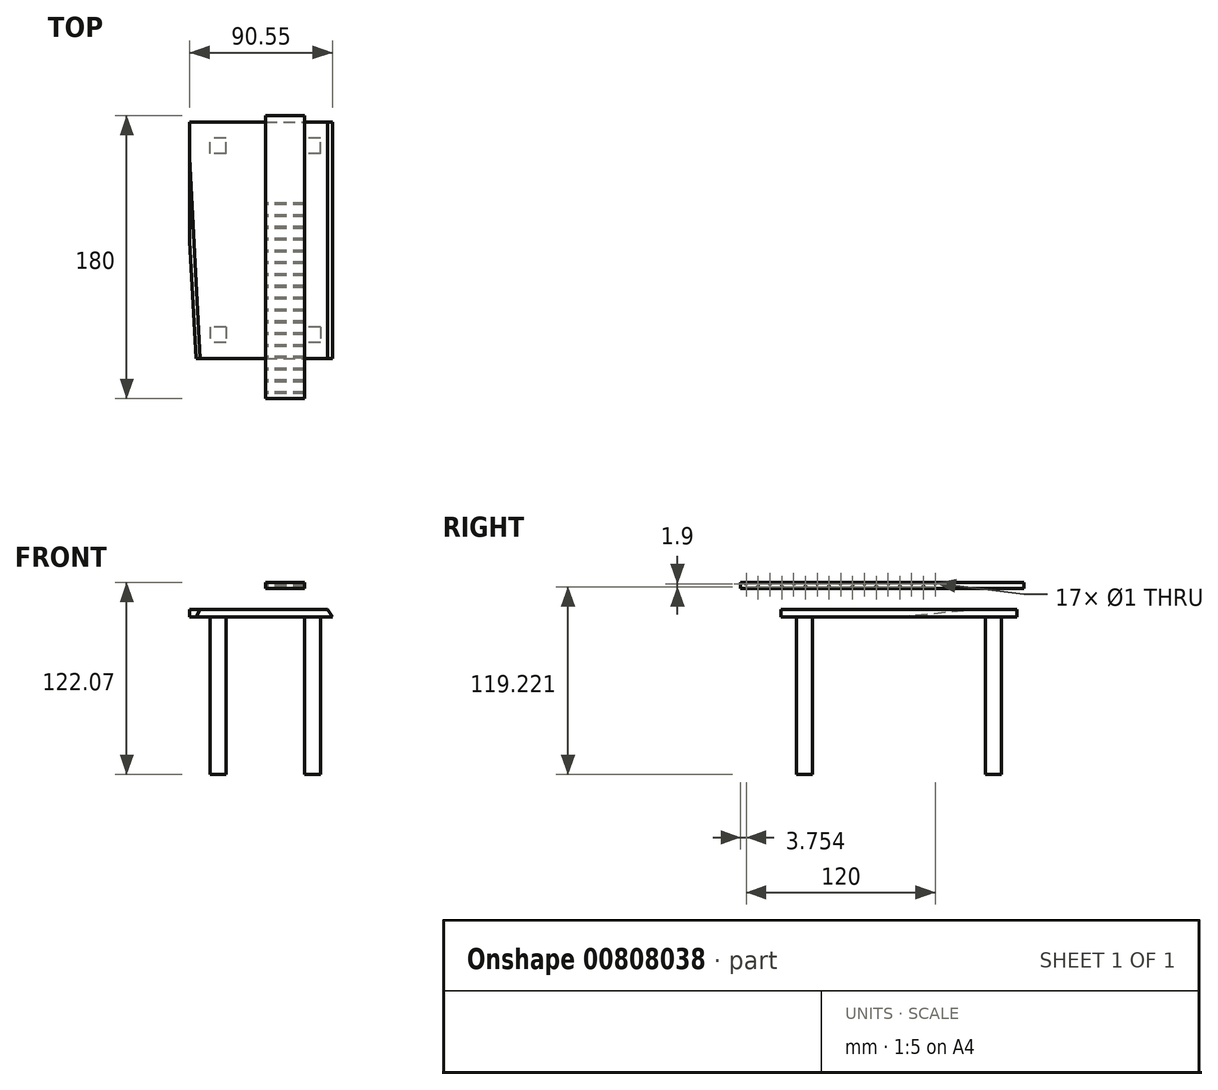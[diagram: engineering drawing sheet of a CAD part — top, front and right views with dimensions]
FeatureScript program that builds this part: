
annotation { "Feature Type Name" : "Feature", "Feature Type Description" : "" }
export const myFeature = defineFeature(function(context is Context, id is Id, definition is map)
    precondition{}
    {
        {
            var Q0;
            Q0=qCreatedBy(makeId("Top.planeOp"),FACE);
            var sketch = newSketch(context, id + "F0", { "sketchPlane" : qUnion([Q0])});
            skLineSegment(sketch, "E0.bottom", {"start": v(0, -75) * mm, "end": v(48, -75) * mm});
            skLineSegment(sketch, "E0.top", {"start": v(0, 75) * mm, "end": v(48, 75) * mm});
            skLineSegment(sketch, "E0.left", {"start": v(0, -75) * mm, "end": v(0, 75) * mm});
            skLineSegment(sketch, "E0.right", {"start": v(48, -75) * mm, "end": v(48, 75) * mm});
            skPoint(sketch, "E0.middle", {"position": v(0, 0) * mm});
            skSolve(sketch);
        }
        {
            var Q0;
            Q0 = qSketchRegion(id + "F0", true);
            extrude(context, id + "F1", {"entities" : qUnion([Q0]), "depth" : 4.8 * mm, "offsetDistance" : 25 * mm});
        }
        {
            var Q0;
            Q0=qCreatedBy(makeId("Top.planeOp"),FACE);
            var sketch = newSketch(context, id + "F2", { "sketchPlane" : qUnion([Q0])});
            skLineSegment(sketch, "E1", {"start": v(48.5, 87.28) * mm, "end": v(40, -75) * mm, "construction": true});
            skLineSegment(sketch, "E2", {"start": v(0, 79.02) * mm, "end": v(0, -87.33) * mm, "construction": true});
            skLineSegment(sketch, "E3", {"start": v(-66.41, -75) * mm, "end": v(-18.41, -75) * mm, "construction": true});
            skSolve(sketch);
        }
        {
            var Q0;
            Q0=sQuery(id+"F2.wireOp",EDGE,"E1");
            cPlane(context, id + "F3", {"entities" : qUnion([Q0]), "cplaneType" : CPlaneType.MID_PLANE, "offset" : 25 * mm, "width" : 150 * mm, "height" : 150 * mm});
        }
        {
            var Q0;
            Q0=qCreatedBy(id+"F3.planeOp",FACE);
            var sketch = newSketch(context, id + "F4", { "sketchPlane" : qUnion([Q0])});
            skLineSegment(sketch, "E4", {"start": v(40.09, 13.64) * mm, "end": v(61.5, 17.13) * mm});
            skLineSegment(sketch, "E5", {"start": v(61.5, 17.13) * mm, "end": v(66.7, -14.02) * mm});
            skLineSegment(sketch, "E6", {"start": v(66.7, -14.02) * mm, "end": v(53.92, -10.31) * mm});
            skLineSegment(sketch, "E7", {"start": v(40.09, 13.64) * mm, "end": v(53.92, -10.31) * mm});
            skSolve(sketch);
        }
        {
            var Q0;
            Q0 = qSketchRegion(id + "F4", true);
            extrude(context, id + "F5", {"entities" : qUnion([Q0]), "operationType" : NewBodyOperationType.REMOVE, "endBound" : BoundingType.THROUGH_ALL, "oppositeDirection" : true, "depth" : 25 * mm, "offsetDistance" : 25 * mm});
        }
        {
            var Q0;
            Q0 = qSketchRegion(id + "F4", true);
            extrude(context, id + "F6", {"entities" : qUnion([Q0]), "operationType" : NewBodyOperationType.REMOVE, "endBound" : BoundingType.THROUGH_ALL, "depth" : 25 * mm, "offsetDistance" : 25 * mm});
        }
        {
            var Q0;
            Q0=makeQuery(id+"F1.opExtrude","SWEPT_BODY",BODY,{"disambiguationData":[OSD([sQuery(id+"F0.wireOp",EDGE,"E0.bottom"),sQuery(id+"F0.wireOp",EDGE,"E0.top"),sQuery(id+"F0.wireOp",EDGE,"E0.left"),sQuery(id+"F0.wireOp",EDGE,"E0.right")])]});
            var Q1;
            Q1=qCreatedBy(makeId("Right.planeOp"),FACE);
            mirror(context, id + "F7", {"operationType" : NewBodyOperationType.ADD, "entities" : qUnion([Q0]), "mirrorPlane" : qUnion([Q1])});
        }
        {
            var Q0;
            {var subQ0=makeQuery(id+"F1.opExtrude","CAP_FACE",FACE,{"disambiguationData":[OSD([sQuery(id+"F0.wireOp",EDGE,"E0.bottom"),sQuery(id+"F0.wireOp",EDGE,"E0.top"),sQuery(id+"F0.wireOp",EDGE,"E0.left"),sQuery(id+"F0.wireOp",EDGE,"E0.right")])],"isStart":true});Q0=makeQuery(id+"F7.boolean.opBoolean","MERGE",FACE,{"derivedFrom":[subQ0,makeQuery(id+"F7.opPattern","COPY",FACE,{"derivedFrom":subQ0,"instanceName":"1"})]});}
            var sketch = newSketch(context, id + "F8", { "sketchPlane" : qUnion([Q0])});
            skLineSegment(sketch, "E8.bottom", {"start": v(30, -60) * mm, "end": v(-30, -60) * mm, "construction": true});
            skLineSegment(sketch, "E8.top", {"start": v(30, 60) * mm, "end": v(-30, 60) * mm, "construction": true});
            skLineSegment(sketch, "E8.left", {"start": v(30, -60) * mm, "end": v(30, 60) * mm, "construction": true});
            skLineSegment(sketch, "E8.right", {"start": v(-30, -60) * mm, "end": v(-30, 60) * mm, "construction": true});
            skPoint(sketch, "E8.middle", {"position": v(0, 0) * mm});
            skLineSegment(sketch, "E9.bottom", {"start": v(-25, 55) * mm, "end": v(-35, 55) * mm});
            skLineSegment(sketch, "E9.top", {"start": v(-25, 65) * mm, "end": v(-35, 65) * mm});
            skLineSegment(sketch, "E9.left", {"start": v(-25, 55) * mm, "end": v(-25, 65) * mm});
            skLineSegment(sketch, "E9.right", {"start": v(-35, 55) * mm, "end": v(-35, 65) * mm});
            skPoint(sketch, "E9.middle", {"position": v(-30, 60) * mm});
            skLineSegment(sketch, "E10.bottom", {"start": v(35, 55) * mm, "end": v(25, 55) * mm});
            skLineSegment(sketch, "E10.top", {"start": v(35, 65) * mm, "end": v(25, 65) * mm});
            skLineSegment(sketch, "E10.left", {"start": v(35, 55) * mm, "end": v(35, 65) * mm});
            skLineSegment(sketch, "E10.right", {"start": v(25, 55) * mm, "end": v(25, 65) * mm});
            skPoint(sketch, "E10.middle", {"position": v(30, 60) * mm});
            skLineSegment(sketch, "E11.bottom", {"start": v(35, -55) * mm, "end": v(25, -55) * mm});
            skLineSegment(sketch, "E11.top", {"start": v(35, -65) * mm, "end": v(25, -65) * mm});
            skLineSegment(sketch, "E11.left", {"start": v(35, -55) * mm, "end": v(35, -65) * mm});
            skLineSegment(sketch, "E11.right", {"start": v(25, -55) * mm, "end": v(25, -65) * mm});
            skPoint(sketch, "E11.middle", {"position": v(30, -60) * mm});
            skLineSegment(sketch, "E12.bottom", {"start": v(-25, -55) * mm, "end": v(-35, -55) * mm});
            skLineSegment(sketch, "E12.top", {"start": v(-25, -65) * mm, "end": v(-35, -65) * mm});
            skLineSegment(sketch, "E12.left", {"start": v(-25, -55) * mm, "end": v(-25, -65) * mm});
            skLineSegment(sketch, "E12.right", {"start": v(-35, -55) * mm, "end": v(-35, -65) * mm});
            skPoint(sketch, "E12.middle", {"position": v(-30, -60) * mm});
            skSolve(sketch);
        }
        {
            var Q0;
            Q0 = qSketchRegion(id + "F8", true);
            extrude(context, id + "F9", {"entities" : qUnion([Q0]), "operationType" : NewBodyOperationType.ADD, "depth" : 100 * mm, "offsetDistance" : 25 * mm});
        }
        {
            var Q0;
            {var subQ0=makeQuery(id+"F1.opExtrude","SWEPT_FACE",FACE,{"disambiguationData":[OSD([sQuery(id+"F0.wireOp",EDGE,"E0.bottom")])]});Q0=makeQuery(id+"F7.boolean.opBoolean","MERGE",FACE,{"derivedFrom":[subQ0,makeQuery(id+"F7.opPattern","COPY",FACE,{"derivedFrom":subQ0,"instanceName":"1"})]});}
            var sketch = newSketch(context, id + "F10", { "sketchPlane" : qUnion([Q0])});
            skLineSegment(sketch, "E13", {"start": v(48.72, -10.13) * mm, "end": v(34.83, 12.68) * mm});
            skLineSegment(sketch, "E14", {"start": v(34.83, 12.68) * mm, "end": v(36.65, 31.45) * mm});
            skLineSegment(sketch, "E15", {"start": v(36.65, 31.45) * mm, "end": v(50.2, 21.12) * mm});
            skLineSegment(sketch, "E16", {"start": v(50.2, 21.12) * mm, "end": v(52.52, -10.3) * mm});
            skLineSegment(sketch, "E17", {"start": v(52.52, -10.3) * mm, "end": v(51.53, -8.98) * mm});
            skLineSegment(sketch, "E18", {"start": v(51.53, -8.98) * mm, "end": v(50.2, -10.46) * mm});
            skLineSegment(sketch, "E19", {"start": v(50.2, -10.46) * mm, "end": v(48.39, -11.95) * mm});
            skLineSegment(sketch, "E20", {"start": v(48.39, -11.95) * mm, "end": v(48.95, -9.76) * mm});
            skLineSegment(sketch, "E21", {"start": v(48.95, -9.76) * mm, "end": v(49, -10.8) * mm});
            skLineSegment(sketch, "E22", {"start": v(49, -10.8) * mm, "end": v(49, -3.85) * mm});
            skLineSegment(sketch, "E23", {"start": v(49, -3.85) * mm, "end": v(48.72, -10.13) * mm});
            skSolve(sketch);
        }
        {
            var Q0;
            Q0 = qSketchRegion(id + "F10", true);
            extrude(context, id + "F11", {"entities" : qUnion([Q0]), "operationType" : NewBodyOperationType.REMOVE, "endBound" : BoundingType.THROUGH_ALL, "oppositeDirection" : true, "depth" : 25 * mm, "offsetDistance" : 25 * mm});
        }
        {
            var Q0;
            Q0=qCreatedBy(makeId("Right.planeOp"),FACE);
            var sketch = newSketch(context, id + "F12", { "sketchPlane" : qUnion([Q0])});
            skLineSegment(sketch, "E24.bottom", {"start": v(-100.67, 22.07) * mm, "end": v(79.33, 22.07) * mm});
            skLineSegment(sketch, "E24.top", {"start": v(-100.67, 18.27) * mm, "end": v(79.33, 18.27) * mm});
            skLineSegment(sketch, "E24.left", {"start": v(-100.67, 22.07) * mm, "end": v(-100.67, 18.27) * mm});
            skLineSegment(sketch, "E24.right", {"start": v(79.33, 22.07) * mm, "end": v(79.33, 18.27) * mm});
            skLineSegment(sketch, "E25", {"start": v(-89.51, 20.17) * mm, "end": v(106.5, 20.17) * mm, "construction": true});
            skLineSegment(sketch, "E26", {"start": v(-86.55, 21.12) * mm, "end": v(118.01, 21.12) * mm, "construction": true});
            skLineSegment(sketch, "E27", {"start": v(-92, 19.22) * mm, "end": v(116.47, 19.22) * mm, "construction": true});
            skCircle(sketch, "E28", {"center": v(-96.92, 21.12) * mm, "radius": 0.5 * mm});
            skCircle(sketch, "E29", {"center": v(-81.92, 21.12) * mm, "radius": 0.5 * mm});
            skCircle(sketch, "E30", {"center": v(-89.42, 19.22) * mm, "radius": 0.5 * mm});
            skCircle(sketch, "E31", {"center": v(-74.42, 19.22) * mm, "radius": 0.5 * mm});
            skCircle(sketch, "E32.1.0.1", {"center": v(-66.92, 21.12) * mm, "radius": 0.5 * mm});
            skLineSegment(sketch, "E32.1.0.2", {"start": v(-71.55, 21.12) * mm, "end": v(133.01, 21.12) * mm, "construction": true});
            skCircle(sketch, "E32.2.0.0", {"center": v(-66.92, 21.12) * mm, "radius": 0.5 * mm});
            skCircle(sketch, "E32.2.0.1", {"center": v(-51.92, 21.12) * mm, "radius": 0.5 * mm});
            skLineSegment(sketch, "E32.2.0.2", {"start": v(-56.55, 21.12) * mm, "end": v(148.01, 21.12) * mm, "construction": true});
            skCircle(sketch, "E32.3.0.0", {"center": v(-51.92, 21.12) * mm, "radius": 0.5 * mm});
            skCircle(sketch, "E32.3.0.1", {"center": v(-36.92, 21.12) * mm, "radius": 0.5 * mm});
            skLineSegment(sketch, "E32.3.0.2", {"start": v(-41.55, 21.12) * mm, "end": v(163.01, 21.12) * mm, "construction": true});
            skCircle(sketch, "E32.4.0.0", {"center": v(-36.92, 21.12) * mm, "radius": 0.5 * mm});
            skCircle(sketch, "E32.4.0.1", {"center": v(-21.92, 21.12) * mm, "radius": 0.5 * mm});
            skLineSegment(sketch, "E32.4.0.2", {"start": v(-26.55, 21.12) * mm, "end": v(178.01, 21.12) * mm, "construction": true});
            skCircle(sketch, "E32.5.0.0", {"center": v(-21.92, 21.12) * mm, "radius": 0.5 * mm});
            skCircle(sketch, "E32.5.0.1", {"center": v(-6.92, 21.12) * mm, "radius": 0.5 * mm});
            skLineSegment(sketch, "E32.5.0.2", {"start": v(-11.55, 21.12) * mm, "end": v(193.01, 21.12) * mm, "construction": true});
            skCircle(sketch, "E32.6.0.0", {"center": v(-6.92, 21.12) * mm, "radius": 0.5 * mm});
            skCircle(sketch, "E32.6.0.1", {"center": v(8.08, 21.12) * mm, "radius": 0.5 * mm});
            skLineSegment(sketch, "E32.6.0.2", {"start": v(3.45, 21.12) * mm, "end": v(208.01, 21.12) * mm, "construction": true});
            skCircle(sketch, "E32.7.0.0", {"center": v(8.08, 21.12) * mm, "radius": 0.5 * mm});
            skCircle(sketch, "E32.7.0.1", {"center": v(23.08, 21.12) * mm, "radius": 0.5 * mm});
            skLineSegment(sketch, "E32.7.0.2", {"start": v(18.45, 21.12) * mm, "end": v(223.01, 21.12) * mm, "construction": true});
            skLineSegment(sketch, "E32.direction1", {"start": v(-81.92, 21.12) * mm, "end": v(-66.92, 21.12) * mm, "construction": true});
            skCircle(sketch, "E33.1.0.0", {"center": v(-59.42, 19.22) * mm, "radius": 0.5 * mm});
            skCircle(sketch, "E33.1.0.1", {"center": v(-44.42, 19.22) * mm, "radius": 0.5 * mm});
            skCircle(sketch, "E33.2.0.0", {"center": v(-29.42, 19.22) * mm, "radius": 0.5 * mm});
            skCircle(sketch, "E33.2.0.1", {"center": v(-14.42, 19.22) * mm, "radius": 0.5 * mm});
            skCircle(sketch, "E33.3.0.0", {"center": v(0.58, 19.22) * mm, "radius": 0.5 * mm});
            skCircle(sketch, "E33.3.0.1", {"center": v(15.58, 19.22) * mm, "radius": 0.5 * mm});
            skLineSegment(sketch, "E33.direction1", {"start": v(-89.42, 19.22) * mm, "end": v(-59.42, 19.22) * mm, "construction": true});
            skSolve(sketch);
        }
        {
            var Q0;
            Q0 = qSketchRegion(id + "F12", true);
            extrude(context, id + "F13", {"entities" : qUnion([Q0]), "depth" : 25 * mm, "offsetDistance" : 25 * mm});
        }
    });
